# Revit family: Domotics-DomesticRanges-GEWISS-SYSTEM_SIGNALLING-LAMP_ANTIBLACKOUT_EXTRACTABLE
name_source: partatom
category: Apparecchi elettrici
revit_build: Autodesk Revit 2016 (Build: 20161004_0715(x64)
units: mm (PartAtom-declared; Revit-internal decimal feet)

## family parameters
Condiviso = Sì
Host = Superficie
Mantenere orientamento annotazione = Sì
Punto di calcolo locali = Sì
Quota connettore circolare = Usa diametro
Taglio con vuoti quando caricato = No
Tipo di parte = Normale

## types (2) — shared parameters
Autonomy = 2H
Carico apparente = 0 VA
Catalogue = DOMOTICS
Catalogue Range = SYSTEM - DOMESTIC RANGE
Description. = Extractable anti black-out lamp
Duration = 2H
Electrocod = 0781
IDF = efd3d5dc-ccee-447b-bb44-d553b1ebb9b0
IDT = 09cab3f6-e541-4a79-a093-1e0089cd254c
Immagine tipo = GW21833.jpg
Lenticular bulb = 2.2V - 0.25 A
N. poli = 1
No. SYSTEM modules = 2
Power supply batteries = Ni-Mh
Produttore = GEWISS S.p.A.
Prospetto di default = 1219 mm
SEO = Lamp
Technical sheet = https://www.gewiss.com
Tipo = System Lampade Antiblack-Out Estraibile_GENERICO : GW21833 Lampada anti black-out est.230V-50Hz nero
Type of lamp = White Led
URL = https://www.gewiss.com
Version file RFA = 19.4
Volt = 230 V

## per-type parameters (varying)
| type | Colour | Descrizione | EAN code | Modello | Supply voltage |
| GW21833 - Remov.emergency lamp 230V-50hz black | Black | REMOV.EMERGENCY LAMP 230V-50HZ SY/BK | 8011564129429 | GW21833 | 230V - 50/60 Hz |
| GW20833 - Remov.emergency lamp 230V-50hz white | White | REMOV.EMERGENCY LAMP 230V-50HZ SY/WT | 8011564054912 | GW20833 | 230 V ac - 50/60 Hz |

## geometry (parser evidence)
native form markers: Sweep x2
no freeform markers — native parametric forms only
